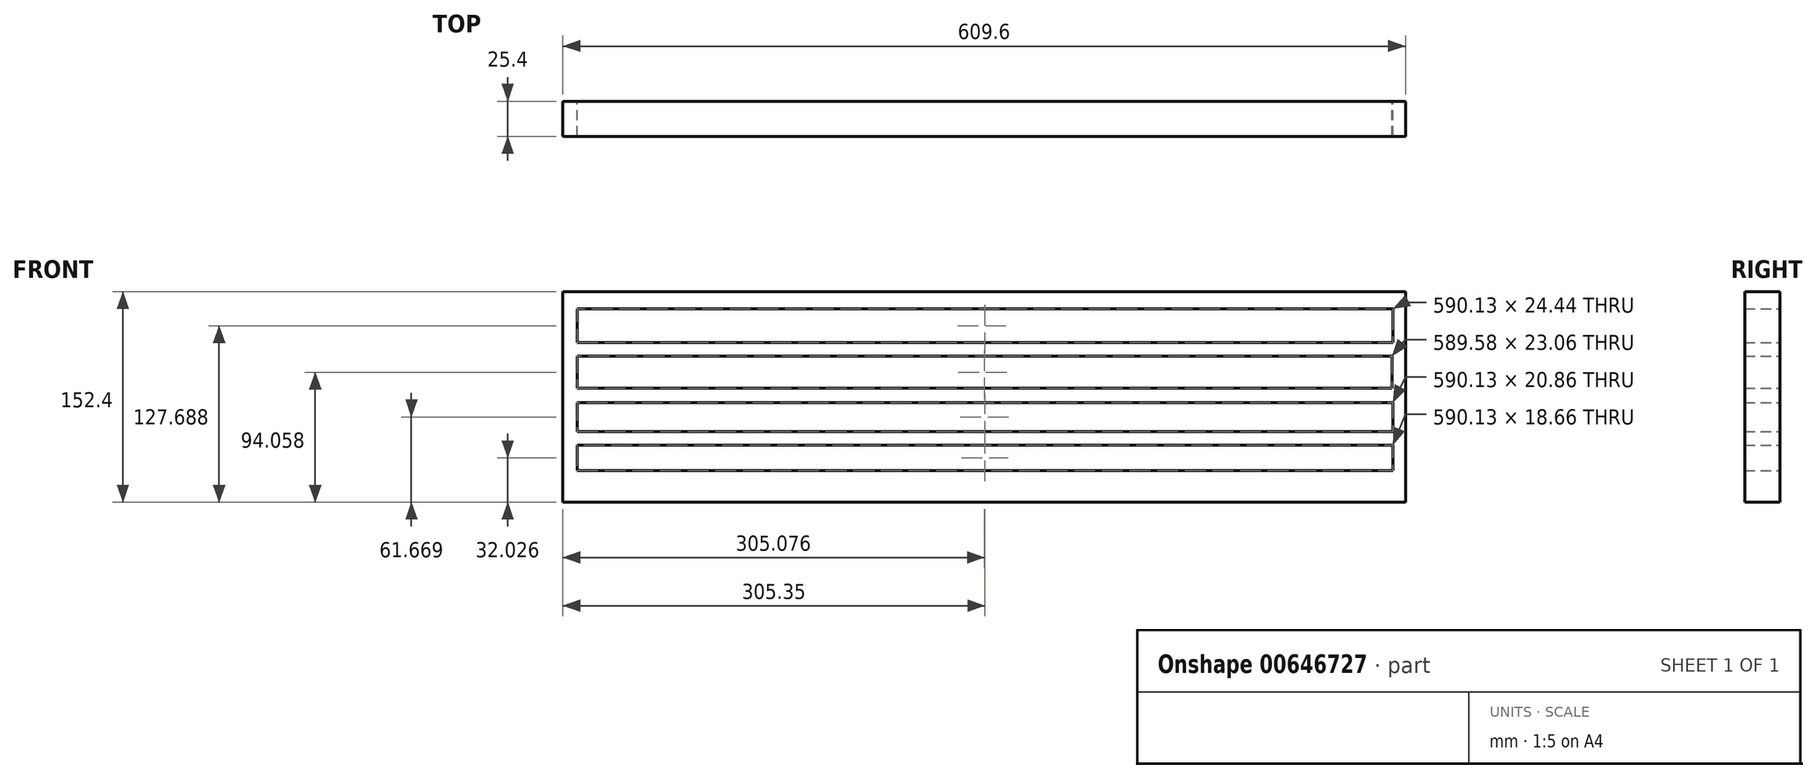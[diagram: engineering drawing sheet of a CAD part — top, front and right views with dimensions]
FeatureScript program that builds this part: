
annotation { "Feature Type Name" : "Feature", "Feature Type Description" : "" }
export const myFeature = defineFeature(function(context is Context, id is Id, definition is map)
    precondition{}
    {
        {
            var Q0;
            Q0=qCreatedBy(makeId("Front.planeOp"),FACE);
            var sketch = newSketch(context, id + "F0", { "sketchPlane" : qUnion([Q0])});
            skLineSegment(sketch, "E0.bottom", {"start": v(-303.65, 12.5) * mm, "end": v(305.95, 12.5) * mm});
            skLineSegment(sketch, "E0.top", {"start": v(-303.65, -139.9) * mm, "end": v(305.95, -139.9) * mm});
            skLineSegment(sketch, "E0.left", {"start": v(-303.65, 12.5) * mm, "end": v(-303.65, -139.9) * mm});
            skLineSegment(sketch, "E0.right", {"start": v(305.95, 12.5) * mm, "end": v(305.95, -139.9) * mm});
            skLineSegment(sketch, "E1.bottom", {"start": v(296.76, 0) * mm, "end": v(-293.36, 0) * mm});
            skLineSegment(sketch, "E1.top", {"start": v(296.76, -24.44) * mm, "end": v(-293.36, -24.44) * mm});
            skLineSegment(sketch, "E1.left", {"start": v(296.76, 0) * mm, "end": v(296.76, -24.44) * mm});
            skLineSegment(sketch, "E1.right", {"start": v(-293.36, 0) * mm, "end": v(-293.36, -24.44) * mm});
            skLineSegment(sketch, "E2.bottom", {"start": v(296.21, -34.32) * mm, "end": v(-293.36, -34.32) * mm});
            skLineSegment(sketch, "E2.top", {"start": v(296.21, -57.38) * mm, "end": v(-293.36, -57.38) * mm});
            skLineSegment(sketch, "E2.left", {"start": v(296.21, -34.32) * mm, "end": v(296.21, -57.38) * mm});
            skLineSegment(sketch, "E2.right", {"start": v(-293.36, -34.32) * mm, "end": v(-293.36, -57.38) * mm});
            skLineSegment(sketch, "E3.bottom", {"start": v(296.76, -67.81) * mm, "end": v(-293.36, -67.81) * mm});
            skLineSegment(sketch, "E3.top", {"start": v(296.76, -88.67) * mm, "end": v(-293.36, -88.67) * mm});
            skLineSegment(sketch, "E3.left", {"start": v(296.76, -67.81) * mm, "end": v(296.76, -88.67) * mm});
            skLineSegment(sketch, "E3.right", {"start": v(-293.36, -67.81) * mm, "end": v(-293.36, -88.67) * mm});
            skLineSegment(sketch, "E4.bottom", {"start": v(296.76, -98.55) * mm, "end": v(-293.36, -98.55) * mm});
            skLineSegment(sketch, "E4.top", {"start": v(296.76, -117.22) * mm, "end": v(-293.36, -117.22) * mm});
            skLineSegment(sketch, "E4.left", {"start": v(296.76, -98.55) * mm, "end": v(296.76, -117.22) * mm});
            skLineSegment(sketch, "E4.right", {"start": v(-293.36, -98.55) * mm, "end": v(-293.36, -117.22) * mm});
            skSolve(sketch);
        }
        {
            var Q0;
            Q0 = qSketchRegion(id + "F0", true);
            extrude(context, id + "F1", {"entities" : qUnion([Q0]), "depth" : 25.4 * mm, "offsetDistance" : 25.4 * mm});
        }
    });
